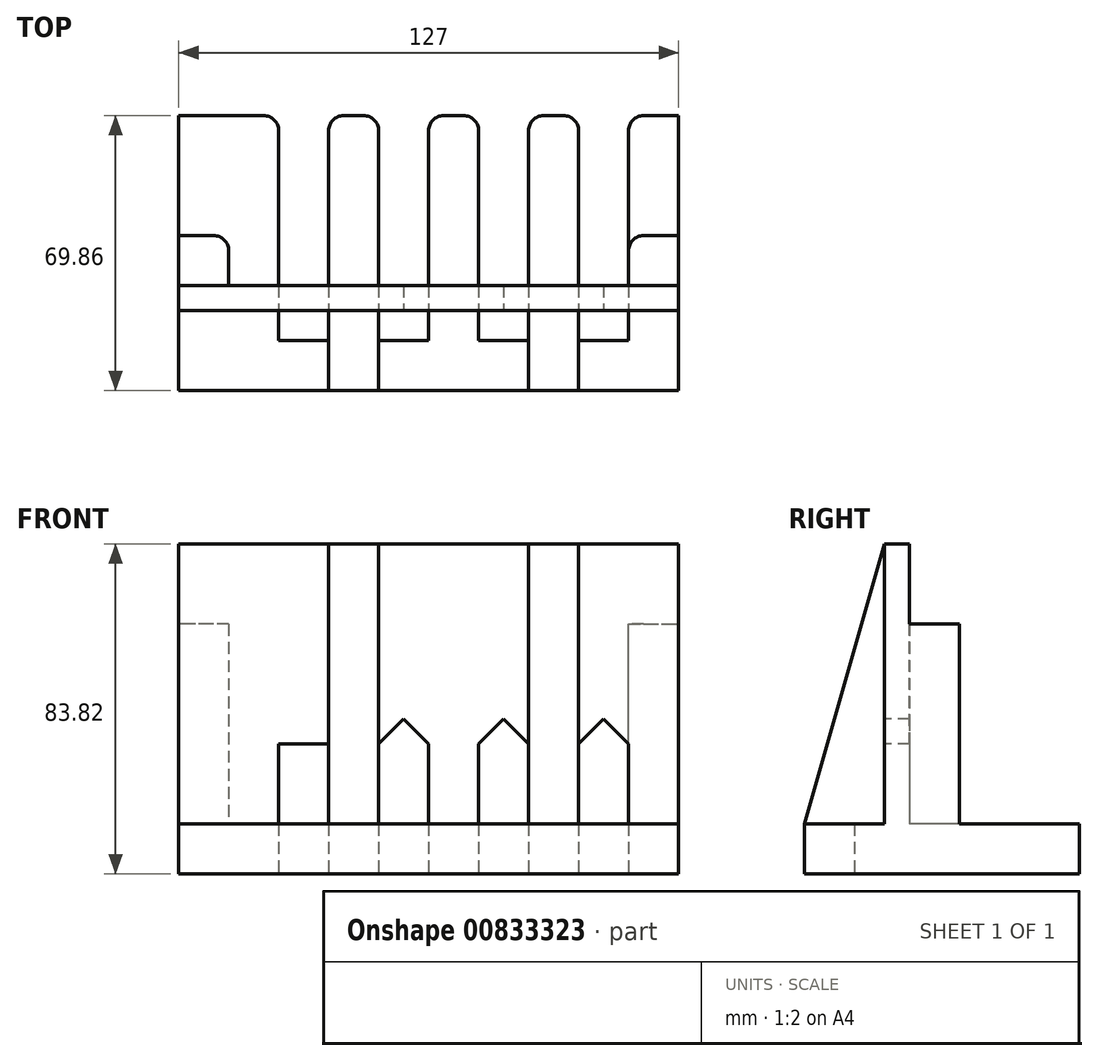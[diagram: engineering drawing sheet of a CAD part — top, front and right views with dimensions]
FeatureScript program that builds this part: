
annotation { "Feature Type Name" : "Feature", "Feature Type Description" : "" }
export const myFeature = defineFeature(function(context is Context, id is Id, definition is map)
    precondition{}
    {
        {
            var Q0;
            Q0=qCreatedBy(makeId("Top.planeOp"),FACE);
            var sketch = newSketch(context, id + "F0", { "sketchPlane" : qUnion([Q0])});
            skLineSegment(sketch, "E0.bottom", {"start": v(63.5, 34.93) * mm, "end": v(50.8, 34.93) * mm});
            skLineSegment(sketch, "E0.top", {"start": v(63.5, -34.92) * mm, "end": v(-63.5, -34.93) * mm});
            skLineSegment(sketch, "E0.left", {"start": v(63.5, 34.93) * mm, "end": v(63.5, -34.92) * mm});
            skLineSegment(sketch, "E0.right", {"start": v(-63.5, 34.92) * mm, "end": v(-63.5, -34.93) * mm});
            skPoint(sketch, "E0.middle", {"position": v(0, 0) * mm});
            skLineSegment(sketch, "E1.top", {"start": v(50.8, -22.22) * mm, "end": v(38.1, -22.22) * mm});
            skLineSegment(sketch, "E1.left", {"start": v(50.8, 34.93) * mm, "end": v(50.8, -22.22) * mm});
            skLineSegment(sketch, "E1.right", {"start": v(38.1, 34.93) * mm, "end": v(38.1, -22.22) * mm});
            skLineSegment(sketch, "E2.top", {"start": v(25.4, -22.22) * mm, "end": v(12.7, -22.22) * mm});
            skLineSegment(sketch, "E2.left", {"start": v(25.4, 34.93) * mm, "end": v(25.4, -22.22) * mm});
            skLineSegment(sketch, "E2.right", {"start": v(12.7, 34.93) * mm, "end": v(12.7, -22.22) * mm});
            skLineSegment(sketch, "E3.top", {"start": v(0, -22.22) * mm, "end": v(-12.7, -22.22) * mm});
            skLineSegment(sketch, "E3.left", {"start": v(0, 34.93) * mm, "end": v(0, -22.22) * mm});
            skLineSegment(sketch, "E3.right", {"start": v(-12.7, 34.93) * mm, "end": v(-12.7, -22.22) * mm});
            skLineSegment(sketch, "E4.trimOffspring", {"start": v(12.7, 34.93) * mm, "end": v(0, 34.93) * mm});
            skLineSegment(sketch, "E5.trimOffspring", {"start": v(-12.7, 34.93) * mm, "end": v(-25.4, 34.93) * mm});
            skLineSegment(sketch, "E6.trimOffspring", {"start": v(38.1, 34.93) * mm, "end": v(25.4, 34.93) * mm});
            skLineSegment(sketch, "E7.top", {"start": v(-25.4, -22.22) * mm, "end": v(-38.1, -22.22) * mm});
            skLineSegment(sketch, "E7.left", {"start": v(-25.4, 34.93) * mm, "end": v(-25.4, -22.22) * mm});
            skLineSegment(sketch, "E7.right", {"start": v(-38.1, 34.92) * mm, "end": v(-38.1, -22.22) * mm});
            skLineSegment(sketch, "E8.top", {"start": v(-50.8, -22.22) * mm, "end": v(-63.5, -22.22) * mm});
            skLineSegment(sketch, "E8.left", {"start": v(-50.8, 34.92) * mm, "end": v(-50.8, -22.22) * mm});
            skLineSegment(sketch, "E8.right", {"start": v(-63.5, 34.92) * mm, "end": v(-63.5, -22.22) * mm});
            skLineSegment(sketch, "E9.trimOffspring", {"start": v(-38.1, 34.93) * mm, "end": v(-50.8, 34.92) * mm});
            skLineSegment(sketch, "E10.bottom", {"start": v(-63.5, 34.92) * mm, "end": v(-50.8, 34.92) * mm});
            skLineSegment(sketch, "E10.top", {"start": v(-63.5, -22.22) * mm, "end": v(-50.8, -22.22) * mm});
            skSolve(sketch);
        }
        {
            var Q0;
            Q0=makeQuery(id+"F0.imprint","IMPRINT",FACE,{"disambiguationData":[TD([[makeQuery(id+"F0.imprint","IMPRINT",EDGE,{"derivedFrom":sQuery(id+"F0.wireOp",EDGE,"E0.bottom")}),1.0]])]});
            var Q1;
            {var subQ2=sQuery(id+"F0.wireOp",EDGE,"E8.top");Q1=makeQuery(id+"F0.imprint","IMPRINT",FACE,{"disambiguationData":[TD([[makeQuery(id+"F0.imprint","IMPRINT",EDGE,{"derivedFrom":subQ2}),-1.0]])]});}
            extrude(context, id + "F1", {"entities" : qUnion([Q0, Q1]), "depth" : 12.7 * mm, "offsetDistance" : 25.4 * mm});
        }
        {
            var Q0;
            Q0=makeQuery(id+"F1.opExtrude","CAP_FACE",FACE,{"disambiguationData":[OSD([sQuery(id+"F0.wireOp",EDGE,"E0.bottom"),sQuery(id+"F0.wireOp",EDGE,"E0.top"),sQuery(id+"F0.wireOp",EDGE,"E0.left"),sQuery(id+"F0.wireOp",EDGE,"E0.right"),sQuery(id+"F0.wireOp",EDGE,"E1.top"),sQuery(id+"F0.wireOp",EDGE,"E1.left"),sQuery(id+"F0.wireOp",EDGE,"E1.right"),sQuery(id+"F0.wireOp",EDGE,"E2.top"),sQuery(id+"F0.wireOp",EDGE,"E2.left"),sQuery(id+"F0.wireOp",EDGE,"E2.right"),sQuery(id+"F0.wireOp",EDGE,"E3.top"),sQuery(id+"F0.wireOp",EDGE,"E3.left"),sQuery(id+"F0.wireOp",EDGE,"E3.right"),sQuery(id+"F0.wireOp",EDGE,"E4.trimOffspring"),sQuery(id+"F0.wireOp",EDGE,"E5.trimOffspring"),sQuery(id+"F0.wireOp",EDGE,"E6.trimOffspring"),sQuery(id+"F0.wireOp",EDGE,"E7.top"),sQuery(id+"F0.wireOp",EDGE,"E7.left"),sQuery(id+"F0.wireOp",EDGE,"E7.right"),sQuery(id+"F0.wireOp",EDGE,"E9.trimOffspring"),sQuery(id+"F0.wireOp",EDGE,"E10.bottom")])],"isStart":false});
            var sketch = newSketch(context, id + "F2", { "sketchPlane" : qUnion([Q0])});
            skLineSegment(sketch, "E11.bottom", {"start": v(-63.5, -8.25) * mm, "end": v(63.5, -8.25) * mm});
            skLineSegment(sketch, "E11.top", {"start": v(-63.5, -14.6) * mm, "end": v(63.5, -14.6) * mm});
            skLineSegment(sketch, "E11.left", {"start": v(-63.5, -8.25) * mm, "end": v(-63.5, -14.6) * mm});
            skLineSegment(sketch, "E11.right", {"start": v(63.5, -8.25) * mm, "end": v(63.5, -14.6) * mm});
            skSolve(sketch);
        }
        {
            var Q0;
            {var subQ0=sQuery(id+"F2.wireOp",EDGE,"E11.right");Q0=makeQuery(id+"F2.imprint","IMPRINT",FACE,{"disambiguationData":[TD([[makeQuery(id+"F2.imprint","IMPRINT",EDGE,{"derivedFrom":subQ0}),-1.0]])]});}
            var Q1;
            {var subQ0=sQuery(id+"F2.wireOp",EDGE,"E11.bottom");var subQ1=makeQuery(id+"F1.opExtrude","CAP_EDGE",EDGE,{"disambiguationData":[OSD([sQuery(id+"F0.wireOp",EDGE,"E7.left")])],"isStart":false});var subQ2=makeQuery(id+"F2.imprint","INTERSECT",VERTEX,{"derivedFrom":[subQ1,subQ0]});Q1=makeQuery(id+"F2.imprint","IMPRINT",FACE,{"disambiguationData":[TD([[makeQuery(id+"F2.imprint","IMPRINT",EDGE,{"disambiguationData":[TD([[subQ2,-1.0]])],"derivedFrom":subQ0}),-1.0]])]});}
            var Q2;
            {var subQ0=sQuery(id+"F2.wireOp",EDGE,"E11.bottom");var subQ1=makeQuery(id+"F1.opExtrude","CAP_EDGE",EDGE,{"disambiguationData":[OSD([sQuery(id+"F0.wireOp",EDGE,"E3.left")])],"isStart":false});var subQ2=makeQuery(id+"F2.imprint","INTERSECT",VERTEX,{"derivedFrom":[subQ1,subQ0]});Q2=makeQuery(id+"F2.imprint","IMPRINT",FACE,{"disambiguationData":[TD([[makeQuery(id+"F2.imprint","IMPRINT",EDGE,{"disambiguationData":[TD([[subQ2,-1.0]])],"derivedFrom":subQ0}),-1.0]])]});}
            var Q3;
            {var subQ0=sQuery(id+"F2.wireOp",EDGE,"E11.bottom");var subQ1=makeQuery(id+"F1.opExtrude","CAP_EDGE",EDGE,{"disambiguationData":[OSD([sQuery(id+"F0.wireOp",EDGE,"E2.left")])],"isStart":false});var subQ2=makeQuery(id+"F2.imprint","INTERSECT",VERTEX,{"derivedFrom":[subQ1,subQ0]});Q3=makeQuery(id+"F2.imprint","IMPRINT",FACE,{"disambiguationData":[TD([[makeQuery(id+"F2.imprint","IMPRINT",EDGE,{"disambiguationData":[TD([[subQ2,-1.0]])],"derivedFrom":subQ0}),-1.0]])]});}
            var Q4;
            {var subQ0=sQuery(id+"F2.wireOp",EDGE,"E11.left");Q4=makeQuery(id+"F2.imprint","IMPRINT",FACE,{"disambiguationData":[TD([[makeQuery(id+"F2.imprint","IMPRINT",EDGE,{"derivedFrom":subQ0}),1.0]])]});}
            extrude(context, id + "F3", {"entities" : qUnion([Q0, Q1, Q2, Q3, Q4]), "operationType" : NewBodyOperationType.ADD, "depth" : 20.32 * mm, "offsetDistance" : 25.4 * mm});
        }
        {
            var Q0;
            Q0=makeQuery(id+"F3.opExtrude","CAP_FACE",FACE,{"disambiguationData":[OSD([sQuery(id+"F0.wireOp",EDGE,"E7.right"),sQuery(id+"F2.wireOp",EDGE,"E11.bottom"),sQuery(id+"F2.wireOp",EDGE,"E11.top"),sQuery(id+"F2.wireOp",EDGE,"E11.left")])],"isStart":false});
            var sketch = newSketch(context, id + "F4", { "sketchPlane" : qUnion([Q0])});
            skLineSegment(sketch, "E12.bottom", {"start": v(-63.5, -8.25) * mm, "end": v(63.5, -8.25) * mm});
            skLineSegment(sketch, "E12.top", {"start": v(-63.5, -14.6) * mm, "end": v(63.5, -14.6) * mm});
            skLineSegment(sketch, "E12.left", {"start": v(-63.5, -8.25) * mm, "end": v(-63.5, -14.6) * mm});
            skLineSegment(sketch, "E12.right", {"start": v(63.5, -8.25) * mm, "end": v(63.5, -14.6) * mm});
            skSolve(sketch);
        }
        {
            var Q0;
            {var subQ0=sQuery(id+"F4.wireOp",EDGE,"E12.left");Q0=makeQuery(id+"F4.imprint","IMPRINT",FACE,{"disambiguationData":[TD([[makeQuery(id+"F4.imprint","IMPRINT",EDGE,{"derivedFrom":subQ0}),1.0]])]});}
            var Q1;
            {var subQ2=sQuery(id+"F4.wireOp",EDGE,"E12.right");Q1=makeQuery(id+"F4.imprint","IMPRINT",FACE,{"disambiguationData":[TD([[makeQuery(id+"F4.imprint","IMPRINT",EDGE,{"derivedFrom":subQ2}),-1.0]])]});}
            var Q2;
            {var subQ2=makeQuery(id+"F3.opExtrude","CAP_EDGE",EDGE,{"disambiguationData":[OSD([sQuery(id+"F0.wireOp",EDGE,"zABGdgFn-UuTn-3QUo-lyOe-LglPwn5iZyxk.right")])],"isStart":false});Q2=makeQuery(id+"F4.imprint","IMPRINT",FACE,{"disambiguationData":[TD([[makeQuery(id+"F4.imprint","IMPRINT",EDGE,{"derivedFrom":subQ2}),-1.0]])]});}
            var Q3;
            {var subQ2=makeQuery(id+"F3.opExtrude","CAP_EDGE",EDGE,{"disambiguationData":[OSD([sQuery(id+"F0.wireOp",EDGE,"23Q52vm6-3tp3-ktcC-OeAA-tuDZzJRh1sQc.left")])],"isStart":false});Q3=makeQuery(id+"F4.imprint","IMPRINT",FACE,{"disambiguationData":[TD([[makeQuery(id+"F4.imprint","IMPRINT",EDGE,{"derivedFrom":subQ2}),-1.0]])]});}
            extrude(context, id + "F5", {"entities" : qUnion([Q0, Q1, Q2, Q3]), "operationType" : NewBodyOperationType.ADD, "depth" : 50.8 * mm, "offsetDistance" : 25.4 * mm});
        }
        {
            var Q0;
            Q0=makeQuery(id+"F5.boolean.opBoolean","MERGE",FACE,{"derivedFrom":[makeQuery(id+"F3.boolean.opBoolean","MERGE",FACE,{"derivedFrom":[makeQuery(id+"F1.opExtrude","SWEPT_FACE",FACE,{"disambiguationData":[OSD([sQuery(id+"F0.wireOp",EDGE,"E0.right")])]}),makeQuery(id+"F3.opExtrude","SWEPT_FACE",FACE,{"disambiguationData":[OSD([sQuery(id+"F2.wireOp",EDGE,"E11.left")])]})]}),makeQuery(id+"F5.opExtrude","SWEPT_FACE",FACE,{"disambiguationData":[OSD([sQuery(id+"F4.wireOp",EDGE,"E12.left")])]})]});
            var sketch = newSketch(context, id + "F6", { "sketchPlane" : qUnion([Q0])});
            skLineSegment(sketch, "E13.bottom", {"start": v(8.25, 12.7) * mm, "end": v(-4.45, 12.7) * mm});
            skLineSegment(sketch, "E13.top", {"start": v(8.25, 63.5) * mm, "end": v(-4.45, 63.5) * mm});
            skLineSegment(sketch, "E13.left", {"start": v(8.25, 12.7) * mm, "end": v(8.25, 63.5) * mm});
            skLineSegment(sketch, "E13.right", {"start": v(-4.45, 12.7) * mm, "end": v(-4.45, 63.5) * mm});
            skSolve(sketch);
        }
        {
            var Q0;
            Q0=makeQuery(id+"F6.imprint","IMPRINT",FACE,{"disambiguationData":[TD([[makeQuery(id+"F6.imprint","IMPRINT",EDGE,{"derivedFrom":sQuery(id+"F6.wireOp",EDGE,"E13.bottom")}),1.0]])]});
            var Q1;
            Q1=makeQuery(id+"F6.imprint","IMPRINT",FACE,{"disambiguationData":[TD([[makeQuery(id+"F6.imprint","IMPRINT",EDGE,{"derivedFrom":sQuery(id+"F6.wireOp",EDGE,"ogDCGRYY-HDVT-Hkr0-qh3N-PnepQPiMfiLJ")}),-1.0]])]});
            extrude(context, id + "F7", {"entities" : qUnion([Q0, Q1]), "operationType" : NewBodyOperationType.ADD, "oppositeDirection" : true, "depth" : 12.7 * mm, "offsetDistance" : 25.4 * mm});
        }
        {
            var Q0;
            {var subQ0=sQuery(id+"F0.wireOp",EDGE,"E3.right");Q0=makeQuery(id+"F3.boolean.opBoolean","MERGE",FACE,{"derivedFrom":[makeQuery(id+"F1.opExtrude","SWEPT_FACE",FACE,{"disambiguationData":[OSD([subQ0])]}),makeQuery(id+"F3.opExtrude","SWEPT_FACE",FACE,{"disambiguationData":[OSD([subQ0])]})]});}
            var sketch = newSketch(context, id + "F8", { "sketchPlane" : qUnion([Q0])});
            skLineSegment(sketch, "E14", {"start": v(-14.6, 83.82) * mm, "end": v(-34.92, 12.7) * mm});
            skLineSegment(sketch, "E15", {"start": v(-34.92, 12.7) * mm, "end": v(-14.6, 12.7) * mm});
            skLineSegment(sketch, "E16", {"start": v(-14.6, 12.7) * mm, "end": v(-14.6, 83.82) * mm});
            skSolve(sketch);
        }
        {
            var Q0;
            {var subQ3=sQuery(id+"F8.wireOp",EDGE,"E14");Q0=makeQuery(id+"F8.imprint","IMPRINT",FACE,{"disambiguationData":[TD([[makeQuery(id+"F8.imprint","IMPRINT",EDGE,{"derivedFrom":subQ3}),1.0]])]});}
            var Q1;
            {var subQ0=sQuery(id+"F0.wireOp",EDGE,"E7.left");Q1=makeQuery(id+"F3.boolean.opBoolean","MERGE",FACE,{"derivedFrom":[makeQuery(id+"F1.opExtrude","SWEPT_FACE",FACE,{"disambiguationData":[OSD([subQ0])]}),makeQuery(id+"F3.opExtrude","SWEPT_FACE",FACE,{"disambiguationData":[OSD([subQ0])]})]});}
            extrude(context, id + "F9", {"entities" : qUnion([Q0]), "operationType" : NewBodyOperationType.ADD, "endBound" : BoundingType.UP_TO_SURFACE, "oppositeDirection" : true, "depth" : 25.4 * mm, "endBoundEntityFace" : qUnion([Q1]), "offsetDistance" : 25.4 * mm});
        }
        {
            var Q0;
            {var subQ0=sQuery(id+"F0.wireOp",EDGE,"E1.right");Q0=makeQuery(id+"F3.boolean.opBoolean","MERGE",FACE,{"derivedFrom":[makeQuery(id+"F1.opExtrude","SWEPT_FACE",FACE,{"disambiguationData":[OSD([subQ0])]}),makeQuery(id+"F3.opExtrude","SWEPT_FACE",FACE,{"disambiguationData":[OSD([subQ0])]})]});}
            var sketch = newSketch(context, id + "F10", { "sketchPlane" : qUnion([Q0])});
            skLineSegment(sketch, "E17", {"start": v(-14.6, 83.82) * mm, "end": v(-14.6, 12.7) * mm});
            skLineSegment(sketch, "E18", {"start": v(-14.6, 12.7) * mm, "end": v(-34.92, 12.7) * mm});
            skLineSegment(sketch, "E19", {"start": v(-34.92, 12.7) * mm, "end": v(-14.6, 83.82) * mm});
            skSolve(sketch);
        }
        {
            var Q0;
            {var subQ5=sQuery(id+"F10.wireOp",EDGE,"E19");Q0=makeQuery(id+"F10.imprint","IMPRINT",FACE,{"disambiguationData":[TD([[makeQuery(id+"F10.imprint","IMPRINT",EDGE,{"derivedFrom":subQ5}),-1.0]])]});}
            var Q1;
            {var subQ0=sQuery(id+"F0.wireOp",EDGE,"E2.left");Q1=makeQuery(id+"F3.boolean.opBoolean","MERGE",FACE,{"derivedFrom":[makeQuery(id+"F1.opExtrude","SWEPT_FACE",FACE,{"disambiguationData":[OSD([subQ0])]}),makeQuery(id+"F3.opExtrude","SWEPT_FACE",FACE,{"disambiguationData":[OSD([subQ0])]})]});}
            extrude(context, id + "F11", {"entities" : qUnion([Q0]), "operationType" : NewBodyOperationType.ADD, "endBound" : BoundingType.UP_TO_SURFACE, "oppositeDirection" : true, "depth" : 25.4 * mm, "endBoundEntityFace" : qUnion([Q1]), "offsetDistance" : 25.4 * mm});
        }
        {
            var Q0;
            Q0=makeQuery(id+"F5.boolean.opBoolean","MERGE",FACE,{"derivedFrom":[makeQuery(id+"F3.boolean.opBoolean","MERGE",FACE,{"derivedFrom":[makeQuery(id+"F1.opExtrude","SWEPT_FACE",FACE,{"disambiguationData":[OSD([sQuery(id+"F0.wireOp",EDGE,"E0.left")])]}),makeQuery(id+"F3.opExtrude","SWEPT_FACE",FACE,{"disambiguationData":[OSD([sQuery(id+"F2.wireOp",EDGE,"E11.right")])]})]}),makeQuery(id+"F5.opExtrude","SWEPT_FACE",FACE,{"disambiguationData":[OSD([sQuery(id+"F4.wireOp",EDGE,"E12.right")])]})]});
            var sketch = newSketch(context, id + "F12", { "sketchPlane" : qUnion([Q0])});
            skLineSegment(sketch, "E20.bottom", {"start": v(4.45, 63.5) * mm, "end": v(-8.26, 63.5) * mm});
            skLineSegment(sketch, "E20.top", {"start": v(4.45, 12.7) * mm, "end": v(-8.25, 12.7) * mm});
            skLineSegment(sketch, "E20.left", {"start": v(4.45, 63.5) * mm, "end": v(4.45, 12.7) * mm});
            skLineSegment(sketch, "E20.right", {"start": v(-8.26, 63.5) * mm, "end": v(-8.25, 12.7) * mm});
            skSolve(sketch);
        }
        {
            var Q0;
            Q0=makeQuery(id+"F12.imprint","IMPRINT",FACE,{"disambiguationData":[TD([[makeQuery(id+"F12.imprint","IMPRINT",EDGE,{"derivedFrom":sQuery(id+"F12.wireOp",EDGE,"E20.bottom")}),1.0]])]});
            var Q1;
            {var subQ0=sQuery(id+"F0.wireOp",EDGE,"E1.left");Q1=makeQuery(id+"F3.boolean.opBoolean","MERGE",FACE,{"derivedFrom":[makeQuery(id+"F1.opExtrude","SWEPT_FACE",FACE,{"disambiguationData":[OSD([subQ0])]}),makeQuery(id+"F3.opExtrude","SWEPT_FACE",FACE,{"disambiguationData":[OSD([subQ0])]})]});}
            extrude(context, id + "F13", {"entities" : qUnion([Q0]), "operationType" : NewBodyOperationType.ADD, "endBound" : BoundingType.UP_TO_SURFACE, "oppositeDirection" : true, "depth" : 25.4 * mm, "endBoundEntityFace" : qUnion([Q1]), "offsetDistance" : 25.4 * mm});
        }
        {
            var Q0;
            Q0=makeQuery(id+"F1.opExtrude","SWEPT_EDGE",EDGE,{"disambiguationData":[OSD([sQuery(id+"F0.wireOp",EDGE,"E0.bottom"),sQuery(id+"F0.wireOp",EDGE,"E1.left")])]});
            var Q1;
            Q1=makeQuery(id+"F1.opExtrude","SWEPT_EDGE",EDGE,{"disambiguationData":[OSD([sQuery(id+"F0.wireOp",EDGE,"E2.left"),sQuery(id+"F0.wireOp",EDGE,"E6.trimOffspring")])]});
            var Q2;
            Q2=makeQuery(id+"F1.opExtrude","SWEPT_EDGE",EDGE,{"disambiguationData":[OSD([sQuery(id+"F0.wireOp",EDGE,"E3.left"),sQuery(id+"F0.wireOp",EDGE,"E4.trimOffspring")])]});
            var Q3;
            Q3=makeQuery(id+"F1.opExtrude","SWEPT_EDGE",EDGE,{"disambiguationData":[OSD([sQuery(id+"F0.wireOp",EDGE,"E5.trimOffspring"),sQuery(id+"F0.wireOp",EDGE,"E7.left")])]});
            var Q4;
            Q4=makeQuery(id+"F1.opExtrude","SWEPT_EDGE",EDGE,{"disambiguationData":[OSD([sQuery(id+"F0.wireOp",EDGE,"E7.right"),sQuery(id+"F0.wireOp",EDGE,"E9.trimOffspring")])]});
            var Q5;
            Q5=makeQuery(id+"F1.opExtrude","SWEPT_EDGE",EDGE,{"disambiguationData":[OSD([sQuery(id+"F0.wireOp",EDGE,"zABGdgFn-UuTn-3QUo-lyOe-LglPwn5iZyxk.left"),sQuery(id+"F0.wireOp",EDGE,"fa87a246-c3c0-417d-bd82-14c914014306.trimOffspring")])]});
            var Q6;
            Q6=makeQuery(id+"F1.opExtrude","SWEPT_EDGE",EDGE,{"disambiguationData":[OSD([sQuery(id+"F0.wireOp",EDGE,"E1.right"),sQuery(id+"F0.wireOp",EDGE,"E6.trimOffspring")])]});
            var Q7;
            Q7=makeQuery(id+"F1.opExtrude","SWEPT_EDGE",EDGE,{"disambiguationData":[OSD([sQuery(id+"F0.wireOp",EDGE,"E2.right"),sQuery(id+"F0.wireOp",EDGE,"E4.trimOffspring")])]});
            var Q8;
            Q8=makeQuery(id+"F1.opExtrude","SWEPT_EDGE",EDGE,{"disambiguationData":[OSD([sQuery(id+"F0.wireOp",EDGE,"E3.right"),sQuery(id+"F0.wireOp",EDGE,"E5.trimOffspring")])]});
            var Q9;
            Q9=makeQuery(id+"F1.opExtrude","SWEPT_EDGE",EDGE,{"disambiguationData":[OSD([sQuery(id+"F0.wireOp",EDGE,"E7.right"),sQuery(id+"F0.wireOp",EDGE,"E9.trimOffspring")])]});
            var Q10;
            Q10=makeQuery(id+"F1.opExtrude","SWEPT_EDGE",EDGE,{"disambiguationData":[OSD([sQuery(id+"F0.wireOp",EDGE,"E8.right"),sQuery(id+"F0.wireOp",EDGE,"fa87a246-c3c0-417d-bd82-14c914014306.trimOffspring")])]});
            var Q11;
            Q11=makeQuery(id+"F1.opExtrude","SWEPT_EDGE",EDGE,{"disambiguationData":[OSD([sQuery(id+"F0.wireOp",EDGE,"zABGdgFn-UuTn-3QUo-lyOe-LglPwn5iZyxk.right"),sQuery(id+"F0.wireOp",EDGE,"a65556d5-ecdc-485d-b082-9fc604778384.trimOffspring")])]});
            var Q12;
            Q12=makeQuery(id+"F1.opExtrude","SWEPT_EDGE",EDGE,{"disambiguationData":[OSD([sQuery(id+"F0.wireOp",EDGE,"23Q52vm6-3tp3-ktcC-OeAA-tuDZzJRh1sQc.right"),sQuery(id+"F0.wireOp",EDGE,"8b2ad57d-cb67-4209-b9d2-ca44a4e64399.trimOffspring")])]});
            var Q13;
            Q13=makeQuery(id+"F1.opExtrude","SWEPT_EDGE",EDGE,{"disambiguationData":[OSD([sQuery(id+"F0.wireOp",EDGE,"a65556d5-ecdc-485d-b082-9fc604778384.trimOffspring"),sQuery(id+"F0.wireOp",EDGE,"23Q52vm6-3tp3-ktcC-OeAA-tuDZzJRh1sQc.left")])]});
            fillet(context, id + "F14", {"entities" : qUnion([Q0, Q1, Q2, Q3, Q4, Q5, Q6, Q7, Q8, Q9, Q10, Q11, Q12, Q13]), "radius" : 3.8 * mm, "tangentPropagation" : true, "allowEdgeOverflow" : false});
        }
        {
            var Q0;
            {var subQ0=sQuery(id+"F0.wireOp",EDGE,"E1.left");var subQ6=sQuery(id+"F0.wireOp",EDGE,"E7.right");var subQ7=sQuery(id+"F0.wireOp",EDGE,"E7.left");var subQ9=sQuery(id+"F0.wireOp",EDGE,"E3.left");var subQ11=sQuery(id+"F0.wireOp",EDGE,"E2.left");var subQ13=sQuery(id+"F0.wireOp",EDGE,"E0.right");var subQ14=sQuery(id+"F0.wireOp",EDGE,"E0.left");var subQ17=makeQuery(id+"F1.opExtrude","SWEPT_FACE",FACE,{"disambiguationData":[OSD([subQ14])]});var subQ19=sQuery(id+"F4.wireOp",EDGE,"E12.top");var subQ31=makeQuery(id+"F1.opExtrude","SWEPT_FACE",FACE,{"disambiguationData":[OSD([subQ11])]});var subQ42=sQuery(id+"F2.wireOp",EDGE,"E11.top");var subQ44=makeQuery(id+"F5.boolean.opBoolean","MERGE",FACE,{"derivedFrom":[makeQuery(id+"F3.opExtrude","SWEPT_FACE",FACE,{"disambiguationData":[OSD([subQ42]),TDD([makeQuery(id+"F2.imprint","IMPRINT",EDGE,{"disambiguationData":[TD([[makeQuery(id+"F2.imprint","INTERSECT",VERTEX,{"derivedFrom":[makeQuery(id+"F1.opExtrude","CAP_EDGE",EDGE,{"disambiguationData":[OSD([subQ6])],"isStart":false}),subQ42]}),1.0]])],"derivedFrom":subQ42})])]}),makeQuery(id+"F3.opExtrude","SWEPT_FACE",FACE,{"disambiguationData":[OSD([subQ42]),TDD([makeQuery(id+"F2.imprint","IMPRINT",EDGE,{"disambiguationData":[TD([[makeQuery(id+"F2.imprint","INTERSECT",VERTEX,{"derivedFrom":[makeQuery(id+"F1.opExtrude","CAP_EDGE",EDGE,{"disambiguationData":[OSD([subQ7])],"isStart":false}),subQ42]}),-1.0]])],"derivedFrom":subQ42})])]}),makeQuery(id+"F3.opExtrude","SWEPT_FACE",FACE,{"disambiguationData":[OSD([subQ42]),TDD([makeQuery(id+"F2.imprint","IMPRINT",EDGE,{"disambiguationData":[TD([[makeQuery(id+"F2.imprint","INTERSECT",VERTEX,{"derivedFrom":[makeQuery(id+"F1.opExtrude","CAP_EDGE",EDGE,{"disambiguationData":[OSD([subQ9])],"isStart":false}),subQ42]}),-1.0]])],"derivedFrom":subQ42})])]}),makeQuery(id+"F3.opExtrude","SWEPT_FACE",FACE,{"disambiguationData":[OSD([subQ42]),TDD([makeQuery(id+"F2.imprint","IMPRINT",EDGE,{"disambiguationData":[TD([[makeQuery(id+"F2.imprint","INTERSECT",VERTEX,{"derivedFrom":[makeQuery(id+"F1.opExtrude","CAP_EDGE",EDGE,{"disambiguationData":[OSD([subQ11])],"isStart":false}),subQ42]}),-1.0]])],"derivedFrom":subQ42})])]}),makeQuery(id+"F3.opExtrude","SWEPT_FACE",FACE,{"disambiguationData":[OSD([subQ42]),TDD([makeQuery(id+"F2.imprint","IMPRINT",EDGE,{"disambiguationData":[TD([[makeQuery(id+"F2.imprint","INTERSECT",VERTEX,{"derivedFrom":[makeQuery(id+"F1.opExtrude","CAP_EDGE",EDGE,{"disambiguationData":[OSD([subQ0])],"isStart":false}),subQ42]}),-1.0]])],"derivedFrom":subQ42})])]}),makeQuery(id+"F5.opExtrude","SWEPT_FACE",FACE,{"disambiguationData":[OSD([subQ19])]})]});var subQ45=makeQuery(id+"F9.boolean.opBoolean","SPLIT",FACE,{"disambiguationData":[TD([subQ17])],"derivedFrom":subQ44});Q0=qUnion([makeQuery(id+"F9.boolean.opBoolean","SPLIT",FACE,{"disambiguationData":[TD([makeQuery(id+"F1.opExtrude","SWEPT_FACE",FACE,{"disambiguationData":[OSD([subQ13])]})])],"derivedFrom":subQ44}),makeQuery(id+"F11.boolean.opBoolean","SPLIT",FACE,{"disambiguationData":[TD([subQ31])],"derivedFrom":subQ45}),makeQuery(id+"F11.boolean.opBoolean","SPLIT",FACE,{"disambiguationData":[TD([subQ17])],"derivedFrom":subQ45})]);}
            var sketch = newSketch(context, id + "F15", { "sketchPlane" : qUnion([Q0])});
            skLineSegment(sketch, "E21.bottom", {"start": v(-25.4, 33.02) * mm, "end": v(-38.1, 33.02) * mm});
            skLineSegment(sketch, "E21.top", {"start": v(-25.4, 39.37) * mm, "end": v(-38.1, 39.37) * mm});
            skLineSegment(sketch, "E21.left", {"start": v(-25.4, 33.02) * mm, "end": v(-25.4, 39.37) * mm});
            skLineSegment(sketch, "E21.right", {"start": v(-38.1, 33.02) * mm, "end": v(-38.1, 39.37) * mm});
            skLineSegment(sketch, "E22.bottom", {"start": v(-38.1, 33.02) * mm, "end": v(-25.4, 33.02) * mm});
            skLineSegment(sketch, "E22.top", {"start": v(-38.1, 39.37) * mm, "end": v(-25.4, 39.37) * mm});
            skLineSegment(sketch, "E23.bottom", {"start": v(-12.7, 33.02) * mm, "end": v(0, 33.02) * mm});
            skLineSegment(sketch, "E23.top", {"start": v(-12.7, 39.37) * mm, "end": v(0, 39.37) * mm});
            skLineSegment(sketch, "E23.left", {"start": v(-12.7, 33.02) * mm, "end": v(-12.7, 39.37) * mm});
            skLineSegment(sketch, "E23.right", {"start": v(0, 33.02) * mm, "end": v(0, 39.37) * mm});
            skLineSegment(sketch, "E24.bottom", {"start": v(12.7, 33.02) * mm, "end": v(25.4, 33.02) * mm});
            skLineSegment(sketch, "E24.top", {"start": v(12.7, 39.37) * mm, "end": v(25.4, 39.37) * mm});
            skLineSegment(sketch, "E24.left", {"start": v(12.7, 33.02) * mm, "end": v(12.7, 39.37) * mm});
            skLineSegment(sketch, "E24.right", {"start": v(25.4, 33.02) * mm, "end": v(25.4, 39.37) * mm});
            skLineSegment(sketch, "E25.bottom", {"start": v(50.8, 33.02) * mm, "end": v(38.1, 33.02) * mm});
            skLineSegment(sketch, "E25.top", {"start": v(50.8, 39.37) * mm, "end": v(38.1, 39.37) * mm});
            skLineSegment(sketch, "E25.left", {"start": v(50.8, 33.02) * mm, "end": v(50.8, 39.37) * mm});
            skLineSegment(sketch, "E25.right", {"start": v(38.1, 33.02) * mm, "end": v(38.1, 39.37) * mm});
            skPoint(sketch, "E26", {"position": v(-31.75, 39.37) * mm});
            skPoint(sketch, "E27", {"position": v(-6.35, 39.37) * mm});
            skPoint(sketch, "E28", {"position": v(19.05, 39.37) * mm});
            skPoint(sketch, "E29", {"position": v(44.45, 39.37) * mm});
            skLineSegment(sketch, "E30", {"start": v(-31.75, 39.37) * mm, "end": v(-38.1, 33.02) * mm});
            skLineSegment(sketch, "E31", {"start": v(-31.75, 39.37) * mm, "end": v(-25.4, 33.02) * mm});
            skLineSegment(sketch, "E32", {"start": v(-6.35, 39.37) * mm, "end": v(-12.7, 33.02) * mm});
            skLineSegment(sketch, "E33", {"start": v(-6.35, 39.37) * mm, "end": v(0, 33.02) * mm});
            skLineSegment(sketch, "E34", {"start": v(19.05, 39.37) * mm, "end": v(12.7, 33.02) * mm});
            skLineSegment(sketch, "E35", {"start": v(19.05, 39.37) * mm, "end": v(25.4, 33.02) * mm});
            skLineSegment(sketch, "E36", {"start": v(44.45, 39.37) * mm, "end": v(38.1, 33.02) * mm});
            skLineSegment(sketch, "E37", {"start": v(44.45, 39.37) * mm, "end": v(50.8, 33.02) * mm});
            skSolve(sketch);
        }
        {
            var Q0;
            Q0=makeQuery(id+"F15.imprint","IMPRINT",FACE,{"disambiguationData":[TD([[makeQuery(id+"F15.imprint","IMPRINT",EDGE,{"derivedFrom":sQuery(id+"F15.wireOp",EDGE,"Z1wcHIoV-O8BE-WRhY-CmVn-MzIPKnQdssG2.bottom")}),1.0]])]});
            var Q1;
            Q1=makeQuery(id+"F15.imprint","IMPRINT",FACE,{"disambiguationData":[TD([[makeQuery(id+"F15.imprint","IMPRINT",EDGE,{"derivedFrom":sQuery(id+"F15.wireOp",EDGE,"E21.bottom")}),-1.0]])]});
            var Q2;
            Q2=makeQuery(id+"F15.imprint","IMPRINT",FACE,{"disambiguationData":[TD([[makeQuery(id+"F15.imprint","IMPRINT",EDGE,{"derivedFrom":sQuery(id+"F15.wireOp",EDGE,"E22.bottom")}),1.0]])]});
            var Q3;
            Q3=makeQuery(id+"F15.imprint","IMPRINT",FACE,{"disambiguationData":[TD([[makeQuery(id+"F15.imprint","IMPRINT",EDGE,{"derivedFrom":sQuery(id+"F15.wireOp",EDGE,"E23.bottom")}),1.0]])]});
            var Q4;
            Q4=makeQuery(id+"F15.imprint","IMPRINT",FACE,{"disambiguationData":[TD([[makeQuery(id+"F15.imprint","IMPRINT",EDGE,{"derivedFrom":sQuery(id+"F15.wireOp",EDGE,"E24.bottom")}),1.0]])]});
            var Q5;
            Q5=makeQuery(id+"F15.imprint","IMPRINT",FACE,{"disambiguationData":[TD([[makeQuery(id+"F15.imprint","IMPRINT",EDGE,{"derivedFrom":sQuery(id+"F15.wireOp",EDGE,"E25.bottom")}),-1.0]])]});
            var Q6;
            Q6=makeQuery(id+"F15.imprint","IMPRINT",FACE,{"disambiguationData":[TD([[makeQuery(id+"F15.imprint","IMPRINT",EDGE,{"derivedFrom":sQuery(id+"F15.wireOp",EDGE,"ec08eXeS-SYfi-1B4N-bpMc-kJDBJBOS7uzN.bottom")}),1.0]])]});
            var Q7;
            Q7=makeQuery(id+"F15.imprint","IMPRINT",FACE,{"disambiguationData":[TD([[makeQuery(id+"F15.imprint","IMPRINT",EDGE,{"derivedFrom":sQuery(id+"F15.wireOp",EDGE,"E25.bottom")}),1.0]])]});
            var Q8;
            {var subQ0=sQuery(id+"F2.wireOp",EDGE,"E11.bottom");Q8=makeQuery(id+"F5.boolean.opBoolean","MERGE",FACE,{"derivedFrom":[makeQuery(id+"F3.opExtrude","SWEPT_FACE",FACE,{"disambiguationData":[OSD([subQ0]),TDD([makeQuery(id+"F2.imprint","IMPRINT",EDGE,{"disambiguationData":[TD([[makeQuery(id+"F2.imprint","INTERSECT",VERTEX,{"derivedFrom":[makeQuery(id+"F1.opExtrude","CAP_EDGE",EDGE,{"disambiguationData":[OSD([sQuery(id+"F0.wireOp",EDGE,"E7.right")])],"isStart":false}),subQ0]}),1.0]])],"derivedFrom":subQ0})])]}),makeQuery(id+"F3.opExtrude","SWEPT_FACE",FACE,{"disambiguationData":[OSD([subQ0]),TDD([makeQuery(id+"F2.imprint","IMPRINT",EDGE,{"disambiguationData":[TD([[makeQuery(id+"F2.imprint","INTERSECT",VERTEX,{"derivedFrom":[makeQuery(id+"F1.opExtrude","CAP_EDGE",EDGE,{"disambiguationData":[OSD([sQuery(id+"F0.wireOp",EDGE,"E7.left")])],"isStart":false}),subQ0]}),-1.0]])],"derivedFrom":subQ0})])]}),makeQuery(id+"F3.opExtrude","SWEPT_FACE",FACE,{"disambiguationData":[OSD([subQ0]),TDD([makeQuery(id+"F2.imprint","IMPRINT",EDGE,{"disambiguationData":[TD([[makeQuery(id+"F2.imprint","INTERSECT",VERTEX,{"derivedFrom":[makeQuery(id+"F1.opExtrude","CAP_EDGE",EDGE,{"disambiguationData":[OSD([sQuery(id+"F0.wireOp",EDGE,"E3.left")])],"isStart":false}),subQ0]}),-1.0]])],"derivedFrom":subQ0})])]}),makeQuery(id+"F3.opExtrude","SWEPT_FACE",FACE,{"disambiguationData":[OSD([subQ0]),TDD([makeQuery(id+"F2.imprint","IMPRINT",EDGE,{"disambiguationData":[TD([[makeQuery(id+"F2.imprint","INTERSECT",VERTEX,{"derivedFrom":[makeQuery(id+"F1.opExtrude","CAP_EDGE",EDGE,{"disambiguationData":[OSD([sQuery(id+"F0.wireOp",EDGE,"E2.left")])],"isStart":false}),subQ0]}),-1.0]])],"derivedFrom":subQ0})])]}),makeQuery(id+"F3.opExtrude","SWEPT_FACE",FACE,{"disambiguationData":[OSD([subQ0]),TDD([makeQuery(id+"F2.imprint","IMPRINT",EDGE,{"disambiguationData":[TD([[makeQuery(id+"F2.imprint","INTERSECT",VERTEX,{"derivedFrom":[makeQuery(id+"F1.opExtrude","CAP_EDGE",EDGE,{"disambiguationData":[OSD([sQuery(id+"F0.wireOp",EDGE,"E1.left")])],"isStart":false}),subQ0]}),-1.0]])],"derivedFrom":subQ0})])]}),makeQuery(id+"F5.opExtrude","SWEPT_FACE",FACE,{"disambiguationData":[OSD([sQuery(id+"F4.wireOp",EDGE,"E12.bottom")])]})]});}
            extrude(context, id + "F16", {"entities" : qUnion([Q0, Q1, Q2, Q3, Q4, Q5, Q6, Q7]), "operationType" : NewBodyOperationType.REMOVE, "endBound" : BoundingType.UP_TO_SURFACE, "oppositeDirection" : true, "depth" : 25.4 * mm, "endBoundEntityFace" : qUnion([Q8]), "offsetDistance" : 25.4 * mm});
        }
        {
            var Q0;
            Q0=makeQuery(id+"F7.opExtrude","CAP_EDGE",EDGE,{"disambiguationData":[OSD([sQuery(id+"F6.wireOp",EDGE,"E13.right")])],"isStart":false});
            var Q1;
            Q1=makeQuery(id+"F13.opExtrude","CAP_EDGE",EDGE,{"disambiguationData":[OSD([sQuery(id+"F12.wireOp",EDGE,"E20.left")])],"isStart":false});
            fillet(context, id + "F17", {"entities" : qUnion([Q0, Q1]), "radius" : 3.8 * mm, "tangentPropagation" : true, "allowEdgeOverflow" : false});
        }
    });
